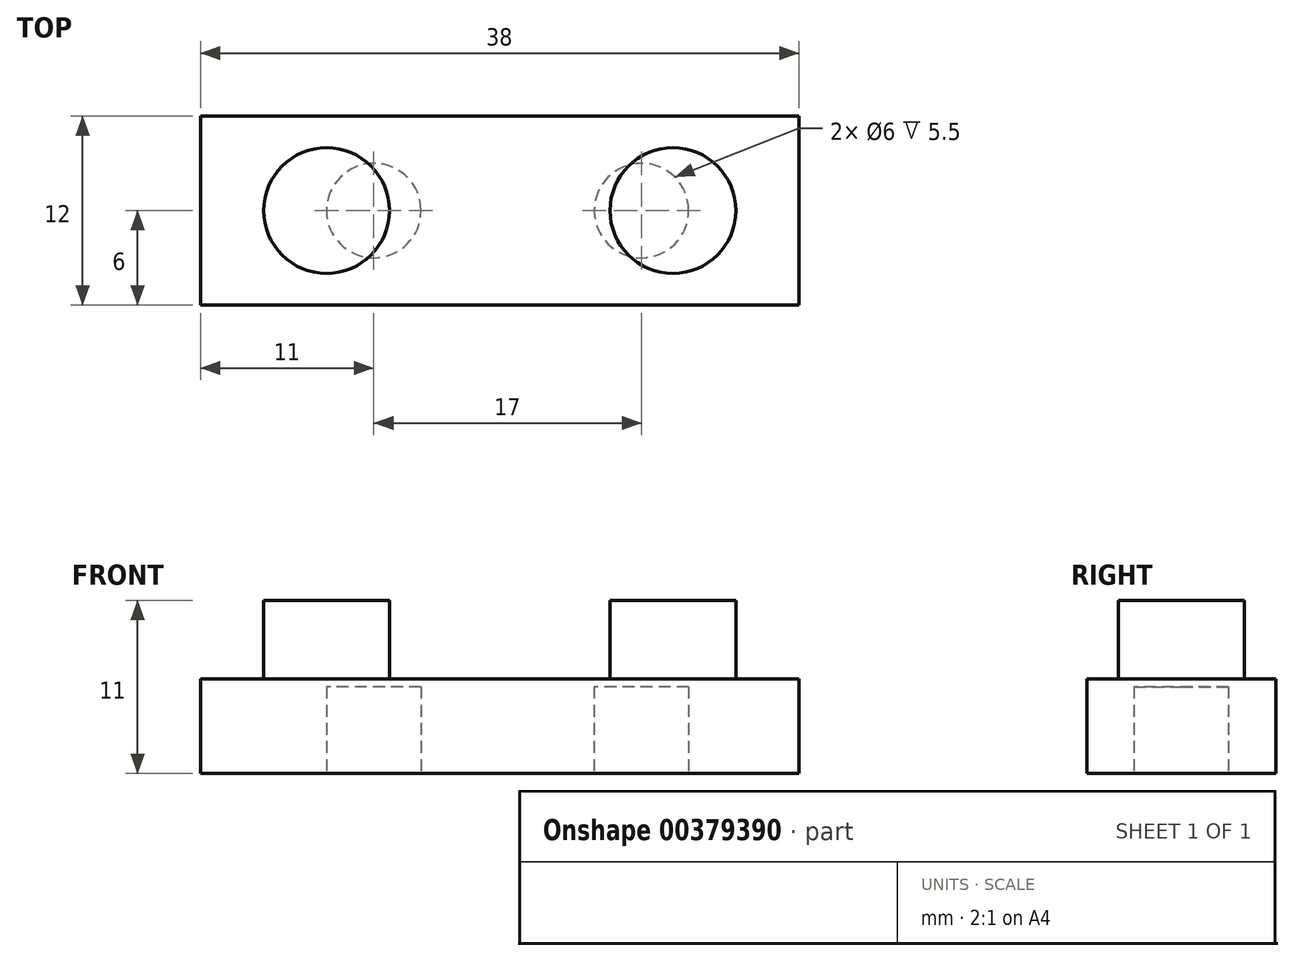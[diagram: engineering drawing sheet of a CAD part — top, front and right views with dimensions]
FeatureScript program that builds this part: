
annotation { "Feature Type Name" : "Feature", "Feature Type Description" : "" }
export const myFeature = defineFeature(function(context is Context, id is Id, definition is map)
    precondition{}
    {
        {
            var Q0;
            Q0=qCreatedBy(makeId("Top.planeOp"),FACE);
            var sketch = newSketch(context, id + "F0", { "sketchPlane" : qUnion([Q0])});
            skLineSegment(sketch, "E0.bottom", {"start": v(0, 0) * mm, "end": v(38, 0) * mm});
            skLineSegment(sketch, "E0.top", {"start": v(0, 12) * mm, "end": v(38, 12) * mm});
            skLineSegment(sketch, "E0.left", {"start": v(0, 0) * mm, "end": v(0, 12) * mm});
            skLineSegment(sketch, "E0.right", {"start": v(38, 0) * mm, "end": v(38, 12) * mm});
            skSolve(sketch);
        }
        {
            var Q0;
            Q0 = qSketchRegion(id + "F0", true);
            extrude(context, id + "F1", {"entities" : qUnion([Q0]), "depth" : 6 * mm});
        }
        {
            var Q0;
            Q0=makeQuery(id+"F1.opExtrude","CAP_FACE",FACE,{"disambiguationData":[OSD([sQuery(id+"F0.wireOp",EDGE,"E0.bottom"),sQuery(id+"F0.wireOp",EDGE,"E0.top"),sQuery(id+"F0.wireOp",EDGE,"E0.left"),sQuery(id+"F0.wireOp",EDGE,"E0.right")])],"isStart":false});
            var sketch = newSketch(context, id + "F2", { "sketchPlane" : qUnion([Q0])});
            skCircle(sketch, "E1", {"center": v(8, 6) * mm, "radius": 4 * mm});
            skSolve(sketch);
        }
        {
            var Q0;
            Q0=makeQuery(id+"F2.imprint","IMPRINT",FACE,{"disambiguationData":[TD([[makeQuery(id+"F2.imprint","IMPRINT",EDGE,{"derivedFrom":sQuery(id+"F2.wireOp",EDGE,"E1")}),1.0]])]});
            var Q1;
            Q1=sQuery(id+"F2.wireOp",EDGE,"E1");
            extrude(context, id + "F3", {"entities" : qUnion([Q0]), "operationType" : NewBodyOperationType.ADD, "surfaceEntities" : qUnion([Q1]), "depth" : 5 * mm});
        }
        {
            var Q0;
            Q0=makeQuery(id+"F1.opExtrude","CAP_FACE",FACE,{"disambiguationData":[OSD([sQuery(id+"F0.wireOp",EDGE,"E0.bottom"),sQuery(id+"F0.wireOp",EDGE,"E0.top"),sQuery(id+"F0.wireOp",EDGE,"E0.left"),sQuery(id+"F0.wireOp",EDGE,"E0.right")])],"isStart":false});
            var sketch = newSketch(context, id + "F4", { "sketchPlane" : qUnion([Q0])});
            skCircle(sketch, "E2", {"center": v(30, 6) * mm, "radius": 4 * mm});
            skSolve(sketch);
        }
        {
            var Q0;
            Q0=makeQuery(id+"F4.imprint","IMPRINT",FACE,{"disambiguationData":[TD([[makeQuery(id+"F4.imprint","IMPRINT",EDGE,{"derivedFrom":sQuery(id+"F4.wireOp",EDGE,"E2")}),1.0]])]});
            var Q1;
            Q1=sQuery(id+"F4.wireOp",EDGE,"E2");
            extrude(context, id + "F5", {"entities" : qUnion([Q0]), "operationType" : NewBodyOperationType.ADD, "surfaceEntities" : qUnion([Q1]), "depth" : 5 * mm});
        }
        {
            var Q0;
            Q0=makeQuery(id+"F0.imprint","IMPRINT",FACE,{"disambiguationData":[TD([[makeQuery(id+"F0.imprint","IMPRINT",EDGE,{"derivedFrom":sQuery(id+"F0.wireOp",EDGE,"E0.bottom")}),1.0]])]});
            var sketch = newSketch(context, id + "F6", { "sketchPlane" : qUnion([Q0])});
            skCircle(sketch, "E3", {"center": v(28, 6) * mm, "radius": 3 * mm});
            skCircle(sketch, "E4", {"center": v(11, 6) * mm, "radius": 3 * mm});
            skSolve(sketch);
        }
        {
            var Q0;
            Q0=makeQuery(id+"F6.imprint","IMPRINT",FACE,{"disambiguationData":[TD([[makeQuery(id+"F6.imprint","IMPRINT",EDGE,{"derivedFrom":sQuery(id+"F6.wireOp",EDGE,"E3")}),1.0]])]});
            var Q1;
            Q1=sQuery(id+"F6.wireOp",EDGE,"E3");
            extrude(context, id + "F7", {"entities" : qUnion([Q0]), "operationType" : NewBodyOperationType.REMOVE, "surfaceEntities" : qUnion([Q1]), "depth" : 5 * mm});
        }
        {
            var Q0;
            Q0 = qSketchRegion(id + "F6", true);
            var Q1;
            Q1=sQuery(id+"F6.wireOp",EDGE,"E4");
            extrude(context, id + "F8", {"entities" : qUnion([Q0]), "operationType" : NewBodyOperationType.REMOVE, "surfaceEntities" : qUnion([Q1]), "depth" : 5.5 * mm});
        }
    });
